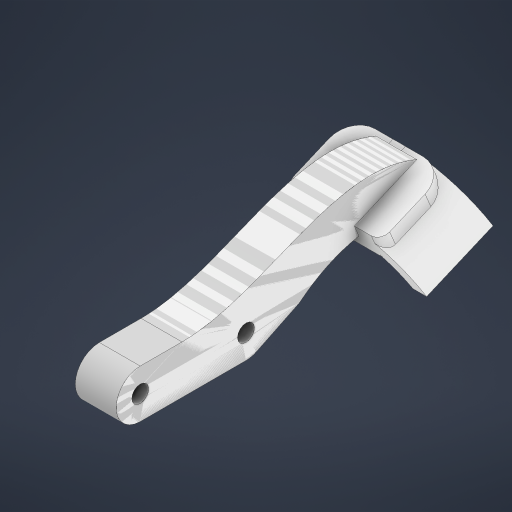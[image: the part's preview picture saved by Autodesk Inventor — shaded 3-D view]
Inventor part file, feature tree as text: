
AUTODESK INVENTOR PART (.ipt)
format: ipt  version: 2024 (Build 280153000, 153)  size: 288,768 bytes
history: native  units: mm
features: extrude x2, fillet x2, sketch x2, other x2
ambient origin geometry x8: Origin, YZ Plane, XZ Plane, XY Plane, X Axis, Y Axis, Z Axis, Center Point
bodies: Solid1 (feature_tree), Solid2 (feature_tree)
feature tree (8):
  extrude  "Extrusion1"  Depth=15.0mm
  fillet  "Fillet1"  Radius=5.0mm
  fillet  "Fillet2"  Radius=2.0mm
  extrude  "Extrusion2"  Depth=15.0mm
  sketch  "Sketch1"  dims[d0=20.0mm d1=15.0mm d2=5.0mm d3=0.0mm d4=2.0mm]
  sketch  "Sketch2"  dims[d5=5.0mm d6=35.0mm d7=10.0mm d8=30.0mm d9=15.0mm d10=0.0mm]
  other  "Boss-Extrude2"
  other  "Boss-Extrude2:1"
